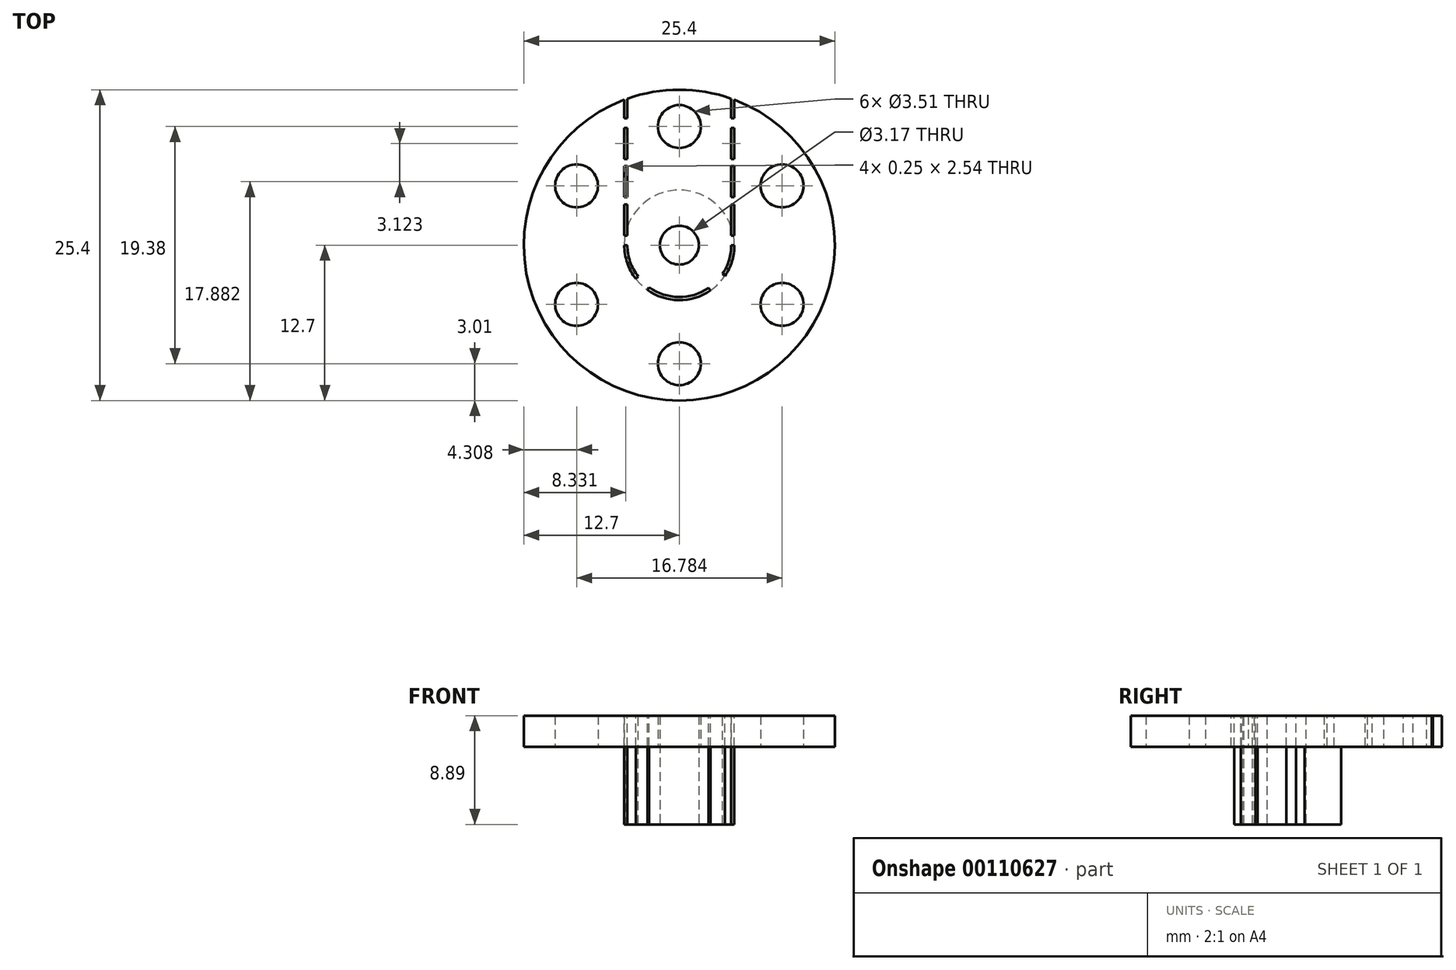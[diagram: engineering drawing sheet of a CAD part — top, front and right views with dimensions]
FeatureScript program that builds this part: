
annotation { "Feature Type Name" : "Feature", "Feature Type Description" : "" }
export const myFeature = defineFeature(function(context is Context, id is Id, definition is map)
    precondition{}
    {
        {
            var Q0;
            Q0=qCreatedBy(makeId("Top.planeOp"),FACE);
            var sketch = newSketch(context, id + "F0", { "sketchPlane" : qUnion([Q0])});
            skCircle(sketch, "E0", {"center": v(0, 0) * mm, "radius": 4.5 * mm});
            skCircle(sketch, "E1", {"center": v(0, 0) * mm, "radius": 1.59 * mm});
            skSolve(sketch);
        }
        {
            var Q0;
            Q0=qSketchRegion(id+"F0",true);
            extrude(context, id + "F1", {"entities" : qUnion([Q0]), "depth" : 6.35 * mm});
        }
        {
            var Q0;
            Q0=makeQuery(id+"F1.opExtrude","CAP_FACE",FACE,{"disambiguationData":[OSD([sQuery(id+"F0.wireOp",EDGE,"E0"),sQuery(id+"F0.wireOp",EDGE,"E1")])],"isStart":false});
            var sketch = newSketch(context, id + "F2", { "sketchPlane" : qUnion([Q0])});
            skCircle(sketch, "E2", {"center": v(0, 0) * mm, "radius": 12.7 * mm});
            skCircle(sketch, "E3", {"center": v(0, 0) * mm, "radius": 1.59 * mm});
            skCircle(sketch, "E4", {"center": v(0, 9.7) * mm, "radius": 1.75 * mm});
            skCircle(sketch, "E5.1.0", {"center": v(-8.4, 4.85) * mm, "radius": 1.75 * mm});
            skCircle(sketch, "E5.2.0", {"center": v(-8.4, -4.85) * mm, "radius": 1.75 * mm});
            skCircle(sketch, "E5.3.0", {"center": v(0, -9.7) * mm, "radius": 1.75 * mm});
            skCircle(sketch, "E5.4.0", {"center": v(8.4, -4.85) * mm, "radius": 1.75 * mm});
            skCircle(sketch, "E5.5.0", {"center": v(8.4, 4.85) * mm, "radius": 1.75 * mm});
            skCircle(sketch, "E6", {"center": v(0, 0) * mm, "radius": 9.7 * mm, "construction": true});
            skSolve(sketch);
        }
        {
            var Q0;
            Q0=qSketchRegion(id+"F2",true);
            extrude(context, id + "F3", {"entities" : qUnion([Q0]), "operationType" : NewBodyOperationType.ADD, "depth" : 2.54 * mm});
        }
        {
            var Q0;
            Q0=makeQuery(id+"F3.opExtrude","CAP_FACE",FACE,{"disambiguationData":[OSD([sQuery(id+"F2.wireOp",EDGE,"E2"),sQuery(id+"F2.wireOp",EDGE,"E3"),sQuery(id+"F2.wireOp",EDGE,"E4"),sQuery(id+"F2.wireOp",EDGE,"E5.1.0"),sQuery(id+"F2.wireOp",EDGE,"E5.2.0"),sQuery(id+"F2.wireOp",EDGE,"E5.3.0"),sQuery(id+"F2.wireOp",EDGE,"E5.4.0"),sQuery(id+"F2.wireOp",EDGE,"E5.5.0")])],"isStart":false});
            var sketch = newSketch(context, id + "F4", { "sketchPlane" : qUnion([Q0])});
            skArc(sketch, "E7", {"start": v(-4.5, 0) * mm, "mid": v(-4.26, -1.45) * mm, "end": v(-3.56, -2.75) * mm});
            skLineSegment(sketch, "E8", {"start": v(-4.5, 9.58) * mm, "end": v(-4.5, 7.04) * mm, "construction": true});
            skLineSegment(sketch, "E9", {"start": v(4.5, 9.58) * mm, "end": v(4.5, 7.04) * mm, "construction": true});
            skLineSegment(sketch, "E10", {"start": v(4.24, 9.58) * mm, "end": v(4.5, 9.58) * mm});
            skLineSegment(sketch, "E11", {"start": v(4.24, 9.58) * mm, "end": v(4.24, 7.04) * mm});
            skLineSegment(sketch, "E12", {"start": v(4.5, 7.04) * mm, "end": v(4.24, 7.04) * mm});
            skLineSegment(sketch, "E13", {"start": v(4.5, 6.45) * mm, "end": v(4.24, 6.45) * mm});
            skLineSegment(sketch, "E14", {"start": v(4.24, 6.45) * mm, "end": v(4.24, 3.91) * mm});
            skArc(sketch, "E15", {"start": v(-2.46, -3.45) * mm, "mid": v(-0.05, -4.24) * mm, "end": v(2.39, -3.5) * mm});
            skLineSegment(sketch, "E16", {"start": v(-4.5, 9.58) * mm, "end": v(-4.24, 9.58) * mm});
            skLineSegment(sketch, "E17", {"start": v(-4.24, 9.58) * mm, "end": v(-4.24, 7.04) * mm});
            skLineSegment(sketch, "E18", {"start": v(-4.24, 7.04) * mm, "end": v(-4.5, 7.04) * mm});
            skLineSegment(sketch, "E19", {"start": v(-4.5, 6.45) * mm, "end": v(-4.24, 6.45) * mm});
            skLineSegment(sketch, "E20", {"start": v(-4.24, 6.45) * mm, "end": v(-4.24, 3.91) * mm});
            skLineSegment(sketch, "E21", {"start": v(-4.24, 3.91) * mm, "end": v(-4.5, 3.91) * mm});
            skLineSegment(sketch, "E22", {"start": v(-4.5, 3.33) * mm, "end": v(-4.24, 3.33) * mm});
            skLineSegment(sketch, "E23", {"start": v(-4.24, 3.33) * mm, "end": v(-4.24, 0.79) * mm});
            skLineSegment(sketch, "E24", {"start": v(-4.24, 0.79) * mm, "end": v(-4.5, 0.79) * mm});
            skLineSegment(sketch, "E25", {"start": v(-4.5, 6.45) * mm, "end": v(-4.5, 3.91) * mm});
            skLineSegment(sketch, "E26", {"start": v(-4.5, 3.33) * mm, "end": v(-4.5, 0.79) * mm});
            skLineSegment(sketch, "E27", {"start": v(-4.5, 7.04) * mm, "end": v(-4.5, 9.58) * mm});
            skLineSegment(sketch, "E28", {"start": v(4.5, 9.58) * mm, "end": v(4.5, 7.04) * mm});
            skLineSegment(sketch, "E29", {"start": v(4.5, 3.91) * mm, "end": v(4.5, 6.45) * mm});
            skLineSegment(sketch, "E30", {"start": v(4.24, 3.91) * mm, "end": v(4.5, 3.91) * mm});
            skLineSegment(sketch, "E31", {"start": v(4.24, 3.33) * mm, "end": v(4.5, 3.33) * mm});
            skLineSegment(sketch, "E32", {"start": v(4.5, 3.33) * mm, "end": v(4.5, 0.79) * mm});
            skLineSegment(sketch, "E33", {"start": v(4.5, 0.79) * mm, "end": v(4.24, 0.79) * mm});
            skLineSegment(sketch, "E34", {"start": v(4.24, 0.79) * mm, "end": v(4.24, 3.33) * mm});
            skLineSegment(sketch, "E35", {"start": v(4.5, 0) * mm, "end": v(4.24, 0) * mm});
            skLineSegment(sketch, "E36", {"start": v(3.73, -2.51) * mm, "end": v(3.53, -2.35) * mm});
            skLineSegment(sketch, "E37", {"start": v(2.55, -3.7) * mm, "end": v(2.39, -3.5) * mm});
            skLineSegment(sketch, "E38", {"start": v(-2.62, -3.66) * mm, "end": v(-2.46, -3.45) * mm});
            skLineSegment(sketch, "E39", {"start": v(-4.5, 0) * mm, "end": v(-4.24, 0) * mm});
            skLineSegment(sketch, "E40", {"start": v(-3.56, -2.75) * mm, "end": v(-3.36, -2.58) * mm});
            skArc(sketch, "E41.trimOffspring", {"start": v(-2.62, -3.66) * mm, "mid": v(-0.04, -4.5) * mm, "end": v(2.55, -3.7) * mm});
            skArc(sketch, "E42.trimOffspring", {"start": v(-4.24, 0) * mm, "mid": v(-4.02, -1.36) * mm, "end": v(-3.36, -2.58) * mm});
            skArc(sketch, "E43.trimOffspring", {"start": v(3.73, -2.51) * mm, "mid": v(4.3, -1.31) * mm, "end": v(4.5, 0) * mm});
            skArc(sketch, "E44.trimOffspring", {"start": v(3.53, -2.35) * mm, "mid": v(4.06, -1.23) * mm, "end": v(4.24, 0) * mm});
            skLineSegment(sketch, "E45.trimOffspring", {"start": v(-4.5, 3.33) * mm, "end": v(-4.5, 0.79) * mm, "construction": true});
            skLineSegment(sketch, "E46.trimOffspring", {"start": v(-4.5, 6.45) * mm, "end": v(-4.5, 3.91) * mm, "construction": true});
            skLineSegment(sketch, "E47.trimOffspring", {"start": v(4.5, 6.45) * mm, "end": v(4.5, 3.91) * mm, "construction": true});
            skLineSegment(sketch, "E48.trimOffspring", {"start": v(4.5, 3.33) * mm, "end": v(4.5, 0.79) * mm, "construction": true});
            skLineSegment(sketch, "E49", {"start": v(-4.5, 10.36) * mm, "end": v(-4.24, 10.36) * mm});
            skLineSegment(sketch, "E50", {"start": v(-4.24, 10.36) * mm, "end": v(-4.24, 11.97) * mm});
            skLineSegment(sketch, "E51", {"start": v(-4.24, 11.97) * mm, "end": v(-4.5, 11.88) * mm});
            skLineSegment(sketch, "E52", {"start": v(-4.5, 11.88) * mm, "end": v(-4.5, 10.36) * mm});
            skLineSegment(sketch, "E53", {"start": v(4.24, 10.36) * mm, "end": v(4.5, 10.36) * mm});
            skLineSegment(sketch, "E54", {"start": v(4.5, 10.36) * mm, "end": v(4.5, 11.88) * mm});
            skLineSegment(sketch, "E55", {"start": v(4.5, 11.88) * mm, "end": v(4.24, 11.97) * mm});
            skLineSegment(sketch, "E56", {"start": v(4.24, 11.97) * mm, "end": v(4.24, 10.36) * mm});
            skSolve(sketch);
        }
        {
            var Q0;
            Q0=qSketchRegion(id+"F4",true);
            extrude(context, id + "F5", {"entities" : qUnion([Q0]), "operationType" : NewBodyOperationType.REMOVE, "oppositeDirection" : true, "depth" : 25.4 * mm});
        }
    });
